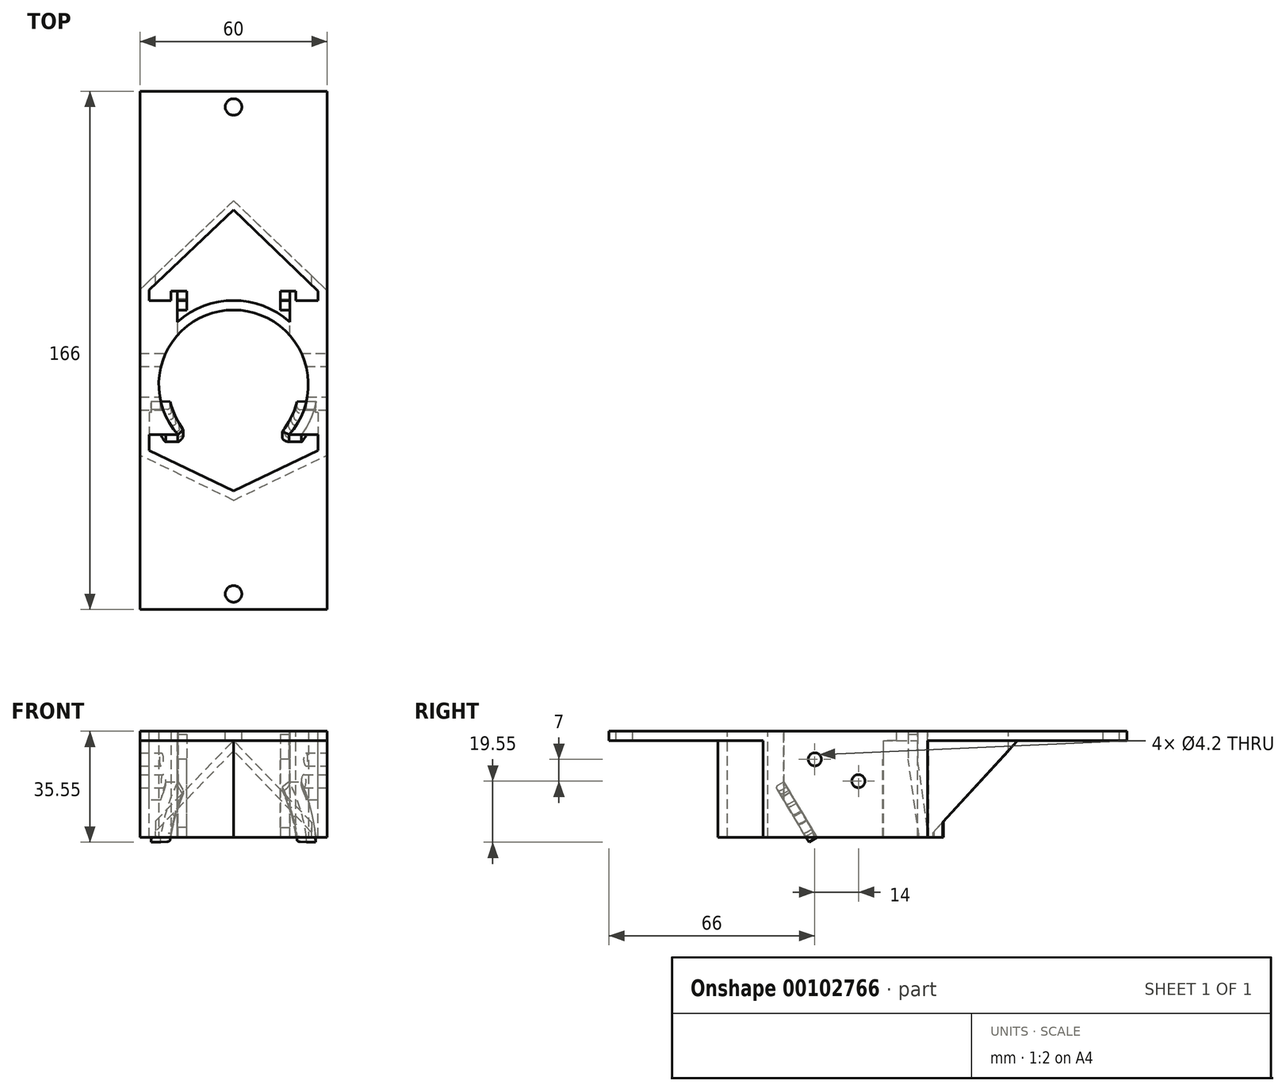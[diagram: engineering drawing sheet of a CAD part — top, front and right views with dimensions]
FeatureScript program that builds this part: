
annotation { "Feature Type Name" : "Feature", "Feature Type Description" : "" }
export const myFeature = defineFeature(function(context is Context, id is Id, definition is map)
    precondition{}
    {
        {
            var Q0;
            Q0=qCreatedBy(makeId("Top.planeOp"),FACE);
            var sketch = newSketch(context, id + "F0", { "sketchPlane" : qUnion([Q0])});
            skArc(sketch, "E0", {"start": v(17.82, -16) * mm, "mid": v(0, 23.95) * mm, "end": v(-17.82, -16) * mm});
            skArc(sketch, "E1", {"start": v(21.75, -16) * mm, "mid": v(0, 27) * mm, "end": v(-21.75, -16) * mm});
            skLineSegment(sketch, "E2", {"start": v(-21.75, -16) * mm, "end": v(-17.82, -16) * mm});
            skLineSegment(sketch, "E3", {"start": v(-17.82, -16) * mm, "end": v(0, -16) * mm, "construction": true});
            skLineSegment(sketch, "E4", {"start": v(0, -16) * mm, "end": v(17.82, -16) * mm, "construction": true});
            skLineSegment(sketch, "E5", {"start": v(17.82, -16) * mm, "end": v(21.75, -16) * mm});
            skLineSegment(sketch, "E6", {"start": v(-39.55, 16) * mm, "end": v(46.97, 16) * mm, "construction": true});
            skLineSegment(sketch, "E7.bottom", {"start": v(-18, 28) * mm, "end": v(18, 28) * mm});
            skLineSegment(sketch, "E7.top", {"start": v(-18, 16) * mm, "end": v(18, 16) * mm});
            skLineSegment(sketch, "E7.left", {"start": v(-18, 28) * mm, "end": v(-18, 16) * mm});
            skLineSegment(sketch, "E7.right", {"start": v(18, 28) * mm, "end": v(18, 16) * mm});
            skLineSegment(sketch, "E8.bottom", {"start": v(-20, 30) * mm, "end": v(20, 30) * mm});
            skLineSegment(sketch, "E8.top", {"start": v(-20, 16) * mm, "end": v(20, 16) * mm});
            skLineSegment(sketch, "E8.left", {"start": v(-20, 30) * mm, "end": v(-20, 16) * mm});
            skLineSegment(sketch, "E8.right", {"start": v(20, 30) * mm, "end": v(20, 16) * mm});
            skLineSegment(sketch, "E9", {"start": v(-18, 28) * mm, "end": v(-18, 30) * mm});
            skLineSegment(sketch, "E10", {"start": v(18, 28) * mm, "end": v(18, 30) * mm});
            skSolve(sketch);
        }
        {
            var Q0;
            {var subQ0=sQuery(id+"F0.wireOp",EDGE,"E5");Q0=makeQuery(id+"F0.imprint","IMPRINT",FACE,{"disambiguationData":[TD([[makeQuery(id+"F0.imprint","IMPRINT",EDGE,{"derivedFrom":subQ0}),1.0]])]});}
            var Q1;
            {var subQ5=sQuery(id+"F0.wireOp",EDGE,"I0pMRqWO-E578-Ecd0-evph-6hkm0RlLLB7E.top");Q1=makeQuery(id+"F0.imprint","IMPRINT",FACE,{"disambiguationData":[TD([[makeQuery(id+"F0.imprint","IMPRINT",EDGE,{"derivedFrom":subQ5}),-1.0]])]});}
            var Q2;
            {var subQ5=sQuery(id+"F0.wireOp",EDGE,"9YEPt3lm-ZwK1-mWlz-v4R1-j5LsX5DvNkkA.top");Q2=makeQuery(id+"F0.imprint","IMPRINT",FACE,{"disambiguationData":[TD([[makeQuery(id+"F0.imprint","IMPRINT",EDGE,{"derivedFrom":subQ5}),1.0]])]});}
            var Q3;
            {var subQ3=sQuery(id+"F0.wireOp",EDGE,"I0pMRqWO-E578-Ecd0-evph-6hkm0RlLLB7E.left");var subQ5=sQuery(id+"F0.wireOp",EDGE,"E1");var subQ6=makeQuery(id+"F0.imprint","INTERSECT",VERTEX,{"derivedFrom":[subQ5,subQ3]});Q3=makeQuery(id+"F0.imprint","IMPRINT",FACE,{"disambiguationData":[TD([[makeQuery(id+"F0.imprint","IMPRINT",EDGE,{"disambiguationData":[TD([[subQ6,-1.0]])],"derivedFrom":subQ5}),1.0]])]});}
            var Q4;
            {var subQ5=sQuery(id+"F0.wireOp",EDGE,"I0pMRqWO-E578-Ecd0-evph-6hkm0RlLLB7E.bottom");Q4=makeQuery(id+"F0.imprint","IMPRINT",FACE,{"disambiguationData":[TD([[makeQuery(id+"F0.imprint","IMPRINT",EDGE,{"derivedFrom":subQ5}),1.0]])]});}
            var Q5;
            {var subQ5=sQuery(id+"F0.wireOp",EDGE,"9YEPt3lm-ZwK1-mWlz-v4R1-j5LsX5DvNkkA.bottom");Q5=makeQuery(id+"F0.imprint","IMPRINT",FACE,{"disambiguationData":[TD([[makeQuery(id+"F0.imprint","IMPRINT",EDGE,{"derivedFrom":subQ5}),-1.0]])]});}
            var Q6;
            {var subQ1=sQuery(id+"F0.wireOp",EDGE,"E2");Q6=makeQuery(id+"F0.imprint","IMPRINT",FACE,{"disambiguationData":[TD([[makeQuery(id+"F0.imprint","IMPRINT",EDGE,{"derivedFrom":subQ1}),1.0]])]});}
            var Q7;
            {var subQ5=sQuery(id+"F0.wireOp",EDGE,"E9");Q7=makeQuery(id+"F0.imprint","IMPRINT",FACE,{"disambiguationData":[TD([[makeQuery(id+"F0.imprint","IMPRINT",EDGE,{"derivedFrom":subQ5}),1.0]])]});}
            var Q8;
            {var subQ5=sQuery(id+"F0.wireOp",EDGE,"E10");Q8=makeQuery(id+"F0.imprint","IMPRINT",FACE,{"disambiguationData":[TD([[makeQuery(id+"F0.imprint","IMPRINT",EDGE,{"derivedFrom":subQ5}),-1.0]])]});}
            var Q9;
            {var subQ0=sQuery(id+"F0.wireOp",EDGE,"E8.top");var subQ8=sQuery(id+"F0.wireOp",EDGE,"E0");var subQ9=makeQuery(id+"F0.imprint","INTERSECT",VERTEX,{"disambiguationData":[OD(0.0)],"derivedFrom":[subQ8,subQ0]});Q9=makeQuery(id+"F0.imprint","IMPRINT",FACE,{"disambiguationData":[TD([[makeQuery(id+"F0.imprint","IMPRINT",EDGE,{"disambiguationData":[TD([[subQ9,-1.0]])],"derivedFrom":subQ8}),-1.0]])]});}
            var Q10;
            {var subQ0=sQuery(id+"F0.wireOp",EDGE,"E8.left");var subQ1=sQuery(id+"F0.wireOp",EDGE,"E1");var subQ2=makeQuery(id+"F0.imprint","INTERSECT",VERTEX,{"derivedFrom":[subQ1,subQ0]});Q10=makeQuery(id+"F0.imprint","IMPRINT",FACE,{"disambiguationData":[TD([[makeQuery(id+"F0.imprint","IMPRINT",EDGE,{"disambiguationData":[TD([[subQ2,1.0]])],"derivedFrom":subQ1}),1.0]])]});}
            var Q11;
            {var subQ0=sQuery(id+"F0.wireOp",EDGE,"E8.right");var subQ1=sQuery(id+"F0.wireOp",EDGE,"E1");var subQ2=makeQuery(id+"F0.imprint","INTERSECT",VERTEX,{"derivedFrom":[subQ1,subQ0]});Q11=makeQuery(id+"F0.imprint","IMPRINT",FACE,{"disambiguationData":[TD([[makeQuery(id+"F0.imprint","IMPRINT",EDGE,{"disambiguationData":[TD([[subQ2,-1.0]])],"derivedFrom":subQ1}),1.0]])]});}
            extrude(context, id + "F1", {"entities" : qUnion([Q0, Q1, Q2, Q3, Q4, Q5, Q6, Q7, Q8, Q9, Q10, Q11]), "depth" : 3 * mm});
        }
        {
            var Q0;
            {var subQ5=sQuery(id+"F0.wireOp",EDGE,"E9");Q0=makeQuery(id+"F0.imprint","IMPRINT",FACE,{"disambiguationData":[TD([[makeQuery(id+"F0.imprint","IMPRINT",EDGE,{"derivedFrom":subQ5}),1.0]])]});}
            var Q1;
            {var subQ5=sQuery(id+"F0.wireOp",EDGE,"E10");Q1=makeQuery(id+"F0.imprint","IMPRINT",FACE,{"disambiguationData":[TD([[makeQuery(id+"F0.imprint","IMPRINT",EDGE,{"derivedFrom":subQ5}),-1.0]])]});}
            var Q2;
            {var subQ0=sQuery(id+"F0.wireOp",EDGE,"E8.left");var subQ1=sQuery(id+"F0.wireOp",EDGE,"E1");var subQ2=makeQuery(id+"F0.imprint","INTERSECT",VERTEX,{"derivedFrom":[subQ1,subQ0]});Q2=makeQuery(id+"F0.imprint","IMPRINT",FACE,{"disambiguationData":[TD([[makeQuery(id+"F0.imprint","IMPRINT",EDGE,{"disambiguationData":[TD([[subQ2,1.0]])],"derivedFrom":subQ1}),1.0]])]});}
            var Q3;
            {var subQ0=sQuery(id+"F0.wireOp",EDGE,"E8.right");var subQ1=sQuery(id+"F0.wireOp",EDGE,"E1");var subQ2=makeQuery(id+"F0.imprint","INTERSECT",VERTEX,{"derivedFrom":[subQ1,subQ0]});Q3=makeQuery(id+"F0.imprint","IMPRINT",FACE,{"disambiguationData":[TD([[makeQuery(id+"F0.imprint","IMPRINT",EDGE,{"disambiguationData":[TD([[subQ2,-1.0]])],"derivedFrom":subQ1}),1.0]])]});}
            extrude(context, id + "F2", {"entities" : qUnion([Q0, Q1, Q2, Q3]), "operationType" : NewBodyOperationType.ADD, "oppositeDirection" : true, "depth" : 6 * mm});
        }
        {
            var Q0;
            Q0=qCreatedBy(makeId("Top.planeOp"),FACE);
            var sketch = newSketch(context, id + "F3", { "sketchPlane" : qUnion([Q0])});
            skLineSegment(sketch, "E11", {"start": v(-34.3, 23.95) * mm, "end": v(29.7, 23.95) * mm, "construction": true});
            skLineSegment(sketch, "E12.bottom", {"start": v(-18, 23.95) * mm, "end": v(-15, 23.95) * mm});
            skLineSegment(sketch, "E12.top", {"start": v(-18, 26.95) * mm, "end": v(-15, 26.95) * mm});
            skLineSegment(sketch, "E12.left", {"start": v(-18, 23.95) * mm, "end": v(-18, 26.95) * mm});
            skLineSegment(sketch, "E12.right", {"start": v(-15, 23.95) * mm, "end": v(-15, 26.95) * mm});
            skLineSegment(sketch, "E13.bottom", {"start": v(15, 23.95) * mm, "end": v(18, 23.95) * mm});
            skLineSegment(sketch, "E13.top", {"start": v(15, 26.95) * mm, "end": v(18, 26.95) * mm});
            skLineSegment(sketch, "E13.left", {"start": v(15, 23.95) * mm, "end": v(15, 26.95) * mm});
            skLineSegment(sketch, "E13.right", {"start": v(18, 23.95) * mm, "end": v(18, 26.95) * mm});
            skSolve(sketch);
        }
        {
            var Q0;
            Q0=makeQuery(id+"F3.imprint","IMPRINT",FACE,{"disambiguationData":[TD([[makeQuery(id+"F3.imprint","IMPRINT",EDGE,{"derivedFrom":sQuery(id+"F3.wireOp",EDGE,"E12.bottom")}),1.0]])]});
            var Q1;
            Q1=makeQuery(id+"F3.imprint","IMPRINT",FACE,{"disambiguationData":[TD([[makeQuery(id+"F3.imprint","IMPRINT",EDGE,{"derivedFrom":sQuery(id+"F3.wireOp",EDGE,"E13.bottom")}),1.0]])]});
            extrude(context, id + "F4", {"entities" : qUnion([Q0, Q1]), "operationType" : NewBodyOperationType.ADD, "depth" : 2 * mm});
        }
        {
            var Q0;
            Q0=makeQuery(id+"F3.imprint","IMPRINT",FACE,{"disambiguationData":[TD([[makeQuery(id+"F3.imprint","IMPRINT",EDGE,{"derivedFrom":sQuery(id+"F3.wireOp",EDGE,"E12.bottom")}),1.0]])]});
            var Q1;
            Q1=makeQuery(id+"F3.imprint","IMPRINT",FACE,{"disambiguationData":[TD([[makeQuery(id+"F3.imprint","IMPRINT",EDGE,{"derivedFrom":sQuery(id+"F3.wireOp",EDGE,"E13.bottom")}),1.0]])]});
            var Q2;
            Q2=makeQuery(id+"F2.opExtrude","CAP_FACE",FACE,{"disambiguationData":[OSD([sQuery(id+"F0.wireOp",EDGE,"E7.left"),sQuery(id+"F0.wireOp",EDGE,"E8.bottom"),sQuery(id+"F0.wireOp",EDGE,"E8.top"),sQuery(id+"F0.wireOp",EDGE,"E8.left"),sQuery(id+"F0.wireOp",EDGE,"E9")])],"isStart":false});
            extrude(context, id + "F5", {"entities" : qUnion([Q0, Q1]), "operationType" : NewBodyOperationType.ADD, "endBound" : BoundingType.UP_TO_SURFACE, "oppositeDirection" : true, "endBoundEntityFace" : qUnion([Q2]), "depth" : 4 * mm});
        }
        {
            var Q0;
            {var subQ0=sQuery(id+"F0.wireOp",EDGE,"E2");Q0=makeQuery(id+"F0.imprint","IMPRINT",FACE,{"disambiguationData":[TD([[makeQuery(id+"F0.imprint","IMPRINT",EDGE,{"derivedFrom":subQ0}),1.0]])]});}
            var Q1;
            {var subQ4=sQuery(id+"F0.wireOp",EDGE,"E5");Q1=makeQuery(id+"F0.imprint","IMPRINT",FACE,{"disambiguationData":[TD([[makeQuery(id+"F0.imprint","IMPRINT",EDGE,{"derivedFrom":subQ4}),1.0]])]});}
            extrude(context, id + "F6", {"entities" : qUnion([Q0, Q1]), "operationType" : NewBodyOperationType.ADD, "oppositeDirection" : true, "depth" : 6 * mm});
        }
        {
            var Q0;
            {var subQ0=sQuery(id+"F0.wireOp",EDGE,"E8.left");Q0=makeQuery(id+"F2.boolean.opBoolean","MERGE",FACE,{"derivedFrom":[makeQuery(id+"F1.opExtrude","SWEPT_FACE",FACE,{"disambiguationData":[OSD([subQ0])]}),makeQuery(id+"F2.opExtrude","SWEPT_FACE",FACE,{"disambiguationData":[OSD([subQ0])]})]});}
            var sketch = newSketch(context, id + "F7", { "sketchPlane" : qUnion([Q0])});
            skLineSegment(sketch, "E14", {"start": v(-23.95, 16.95) * mm, "end": v(-23.95, -28.82) * mm, "construction": true});
            skLineSegment(sketch, "E15.bottom", {"start": v(-30, -6) * mm, "end": v(-18.14, -6) * mm});
            skLineSegment(sketch, "E15.top", {"start": v(-30, -31) * mm, "end": v(-18.14, -31) * mm});
            skLineSegment(sketch, "E15.left", {"start": v(-30, -6) * mm, "end": v(-30, -31) * mm});
            skLineSegment(sketch, "E15.right", {"start": v(-18.14, -6) * mm, "end": v(-18.14, -31) * mm});
            skLineSegment(sketch, "E16", {"start": v(-27.45, 14.9) * mm, "end": v(-27.45, -40.68) * mm, "construction": true});
            skLineSegment(sketch, "E17", {"start": v(-23.95, -6) * mm, "end": v(-27.45, -31) * mm});
            skLineSegment(sketch, "E18", {"start": v(-26.95, -6) * mm, "end": v(-30.45, -31) * mm});
            skLineSegment(sketch, "E19", {"start": v(-30.45, -31) * mm, "end": v(-30, -31) * mm});
            skSolve(sketch);
        }
        {
            var Q0;
            {var subQ0=sQuery(id+"F7.wireOp",EDGE,"E17");Q0=makeQuery(id+"F7.imprint","IMPRINT",FACE,{"disambiguationData":[TD([[makeQuery(id+"F7.imprint","IMPRINT",EDGE,{"derivedFrom":subQ0}),-1.0]])]});}
            var Q1;
            {var subQ0=sQuery(id+"F3.wireOp",EDGE,"E12.right");Q1=makeQuery(id+"F5.boolean.opBoolean","MERGE",FACE,{"derivedFrom":[makeQuery(id+"F4.opExtrude","SWEPT_FACE",FACE,{"disambiguationData":[OSD([subQ0])]}),makeQuery(id+"F5.opExtrude","SWEPT_FACE",FACE,{"disambiguationData":[OSD([subQ0])]})]});}
            extrude(context, id + "F8", {"entities" : qUnion([Q0]), "operationType" : NewBodyOperationType.ADD, "endBound" : BoundingType.UP_TO_SURFACE, "oppositeDirection" : true, "endBoundEntityFace" : qUnion([Q1]), "depth" : 25 * mm});
        }
        {
            var Q0;
            {var subQ0=sQuery(id+"F7.wireOp",EDGE,"E15.right");Q0=makeQuery(id+"F7.imprint","IMPRINT",FACE,{"disambiguationData":[TD([[makeQuery(id+"F7.imprint","IMPRINT",EDGE,{"derivedFrom":subQ0}),-1.0]])]});}
            var Q1;
            {var subQ1=sQuery(id+"F7.wireOp",EDGE,"E15.bottom");var subQ5=sQuery(id+"F7.wireOp",EDGE,"E18");var subQ6=makeQuery(id+"F7.imprint","INTERSECT",VERTEX,{"derivedFrom":[subQ1,subQ5]});Q1=makeQuery(id+"F7.imprint","IMPRINT",FACE,{"disambiguationData":[TD([[makeQuery(id+"F7.imprint","IMPRINT",EDGE,{"disambiguationData":[TD([[subQ6,-1.0]])],"derivedFrom":subQ5}),-1.0]])]});}
            var Q2;
            {var subQ0=sQuery(id+"F7.wireOp",EDGE,"E17");Q2=makeQuery(id+"F7.imprint","IMPRINT",FACE,{"disambiguationData":[TD([[makeQuery(id+"F7.imprint","IMPRINT",EDGE,{"derivedFrom":subQ0}),-1.0]])]});}
            extrude(context, id + "F9", {"entities" : qUnion([Q0, Q1, Q2]), "operationType" : NewBodyOperationType.ADD, "oppositeDirection" : true, "depth" : 2 * mm});
        }
        {
            var Q0;
            {var subQ0=sQuery(id+"F0.wireOp",EDGE,"E8.right");Q0=makeQuery(id+"F2.boolean.opBoolean","MERGE",FACE,{"derivedFrom":[makeQuery(id+"F1.opExtrude","SWEPT_FACE",FACE,{"disambiguationData":[OSD([subQ0])]}),makeQuery(id+"F2.opExtrude","SWEPT_FACE",FACE,{"disambiguationData":[OSD([subQ0])]})]});}
            var sketch = newSketch(context, id + "F10", { "sketchPlane" : qUnion([Q0])});
            skLineSegment(sketch, "E20", {"start": v(23.95, -6) * mm, "end": v(27.45, -31) * mm});
            skLineSegment(sketch, "E21", {"start": v(27.45, -31) * mm, "end": v(30.45, -31) * mm});
            skLineSegment(sketch, "E22", {"start": v(30.45, -31) * mm, "end": v(26.95, -6) * mm});
            skLineSegment(sketch, "E23", {"start": v(26.95, -6) * mm, "end": v(23.95, -6) * mm});
            skLineSegment(sketch, "E24.bottom", {"start": v(18.14, -6) * mm, "end": v(30, -6) * mm});
            skLineSegment(sketch, "E24.top", {"start": v(18.14, -31) * mm, "end": v(30, -31) * mm});
            skLineSegment(sketch, "E24.left", {"start": v(18.14, -6) * mm, "end": v(18.14, -31) * mm});
            skLineSegment(sketch, "E24.right", {"start": v(30, -6) * mm, "end": v(30, -31) * mm});
            skSolve(sketch);
        }
        {
            var Q0;
            {var subQ0=sQuery(id+"F10.wireOp",EDGE,"E20");Q0=makeQuery(id+"F10.imprint","IMPRINT",FACE,{"disambiguationData":[TD([[makeQuery(id+"F10.imprint","IMPRINT",EDGE,{"derivedFrom":subQ0}),-1.0]])]});}
            var Q1;
            {var subQ1=sQuery(id+"F10.wireOp",EDGE,"E20");Q1=makeQuery(id+"F10.imprint","IMPRINT",FACE,{"disambiguationData":[TD([[makeQuery(id+"F10.imprint","IMPRINT",EDGE,{"derivedFrom":subQ1}),1.0]])]});}
            var Q2;
            {var subQ0=sQuery(id+"F10.wireOp",EDGE,"E24.bottom");var subQ1=sQuery(id+"F10.wireOp",EDGE,"E22");var subQ2=makeQuery(id+"F10.imprint","INTERSECT",VERTEX,{"derivedFrom":[subQ1,subQ0]});Q2=makeQuery(id+"F10.imprint","IMPRINT",FACE,{"disambiguationData":[TD([[makeQuery(id+"F10.imprint","IMPRINT",EDGE,{"disambiguationData":[TD([[subQ2,1.0]])],"derivedFrom":subQ1}),-1.0]])]});}
            var Q3;
            {var subQ0=sQuery(id+"F0.wireOp",EDGE,"E10");var subQ1=sQuery(id+"F0.wireOp",EDGE,"E7.right");Q3=makeQuery(id+"F2.boolean.opBoolean","MERGE",FACE,{"derivedFrom":[makeQuery(id+"F1.opExtrude","SWEPT_FACE",FACE,{"disambiguationData":[OSD([subQ1,subQ0])]}),makeQuery(id+"F2.opExtrude","SWEPT_FACE",FACE,{"disambiguationData":[OSD([subQ1,subQ0])]})]});}
            extrude(context, id + "F11", {"entities" : qUnion([Q0, Q1, Q2]), "operationType" : NewBodyOperationType.ADD, "endBound" : BoundingType.UP_TO_SURFACE, "oppositeDirection" : true, "endBoundEntityFace" : qUnion([Q3]), "depth" : 25 * mm});
        }
        {
            var Q0;
            {var subQ1=sQuery(id+"F10.wireOp",EDGE,"E20");Q0=makeQuery(id+"F10.imprint","IMPRINT",FACE,{"disambiguationData":[TD([[makeQuery(id+"F10.imprint","IMPRINT",EDGE,{"derivedFrom":subQ1}),1.0]])]});}
            var Q1;
            {var subQ0=sQuery(id+"F3.wireOp",EDGE,"E13.left");Q1=makeQuery(id+"F5.boolean.opBoolean","MERGE",FACE,{"derivedFrom":[makeQuery(id+"F4.opExtrude","SWEPT_FACE",FACE,{"disambiguationData":[OSD([subQ0])]}),makeQuery(id+"F5.opExtrude","SWEPT_FACE",FACE,{"disambiguationData":[OSD([subQ0])]})]});}
            extrude(context, id + "F12", {"entities" : qUnion([Q0]), "operationType" : NewBodyOperationType.ADD, "endBound" : BoundingType.UP_TO_SURFACE, "oppositeDirection" : true, "endBoundEntityFace" : qUnion([Q1]), "depth" : 25 * mm});
        }
        {
            var Q0;
            {var subQ0=sQuery(id+"F0.wireOp",EDGE,"E0");var subQ1=sQuery(id+"F0.wireOp",EDGE,"E8.top");var subQ2=sQuery(id+"F3.wireOp",EDGE,"E12.bottom");var subQ3=sQuery(id+"F0.wireOp",EDGE,"E8.left");var subQ4=sQuery(id+"F0.wireOp",EDGE,"E9");var subQ5=sQuery(id+"F0.wireOp",EDGE,"E7.left");var subQ6=sQuery(id+"F0.wireOp",EDGE,"E2");var subQ7=sQuery(id+"F0.wireOp",EDGE,"E1");var subQ12=sQuery(id+"F0.wireOp",EDGE,"E8.bottom");Q0=makeQuery(id+"F8.boolean.opBoolean","SPLIT",FACE,{"disambiguationData":[TD([makeQuery(id+"F1.opExtrude","SWEPT_FACE",FACE,{"disambiguationData":[OSD([subQ0])]})])],"derivedFrom":makeQuery(id+"F6.boolean.opBoolean","MERGE",FACE,{"derivedFrom":[makeQuery(id+"F5.boolean.opBoolean","MERGE",FACE,{"derivedFrom":[makeQuery(id+"F2.opExtrude","CAP_FACE",FACE,{"disambiguationData":[OSD([subQ5,subQ12,subQ1,subQ3,subQ4])],"isStart":false}),makeQuery(id+"F5.opExtrude","CAP_FACE",FACE,{"disambiguationData":[OSD([subQ5,subQ12,subQ1,subQ3,subQ4]),ownerDisambiguation([makeQuery(id+"F5.opExtrude","SWEPT_BODY",BODY,{"disambiguationData":[OSD([subQ2,sQuery(id+"F3.wireOp",EDGE,"E12.top"),sQuery(id+"F3.wireOp",EDGE,"E12.left"),sQuery(id+"F3.wireOp",EDGE,"E12.right")])]})])],"isStart":false})]}),makeQuery(id+"F6.opExtrude","CAP_FACE",FACE,{"disambiguationData":[OSD([subQ0,subQ7,subQ6,subQ1,subQ3])],"isStart":false})]})});}
            var sketch = newSketch(context, id + "F13", { "sketchPlane" : qUnion([Q0])});
            skArc(sketch, "E25", {"start": v(-17.82, 16) * mm, "mid": v(-23.9, -1.53) * mm, "end": v(-15.64, -18.14) * mm});
            skArc(sketch, "E26", {"start": v(-21.75, 16) * mm, "mid": v(-26.96, -1.38) * mm, "end": v(-20, -18.14) * mm});
            skLineSegment(sketch, "E27", {"start": v(-36.94, 16) * mm, "end": v(37.61, 16) * mm, "construction": true});
            skLineSegment(sketch, "E28", {"start": v(-44, -18.14) * mm, "end": v(46.28, -18.14) * mm, "construction": true});
            skArc(sketch, "E29.trimOffspring", {"start": v(15.64, -18.14) * mm, "mid": v(23.9, -1.53) * mm, "end": v(17.82, 16) * mm});
            skArc(sketch, "E30.trimOffspring", {"start": v(20, -18.14) * mm, "mid": v(26.96, -1.38) * mm, "end": v(21.75, 16) * mm});
            skLineSegment(sketch, "E31", {"start": v(-21.75, 16) * mm, "end": v(-17.82, 16) * mm});
            skLineSegment(sketch, "E32", {"start": v(17.82, 16) * mm, "end": v(21.75, 16) * mm});
            skLineSegment(sketch, "E33", {"start": v(15.64, -18.14) * mm, "end": v(20, -18.14) * mm});
            skLineSegment(sketch, "E34", {"start": v(-20, -18.14) * mm, "end": v(-15.64, -18.14) * mm});
            skLineSegment(sketch, "E35", {"start": v(18, -14.37) * mm, "end": v(18, -22.26) * mm});
            skSolve(sketch);
        }
        {
            var Q0;
            {var subQ1=sQuery(id+"F13.wireOp",EDGE,"E30.trimOffspring");Q0=makeQuery(id+"F13.imprint","IMPRINT",FACE,{"disambiguationData":[TD([[makeQuery(id+"F13.imprint","IMPRINT",EDGE,{"derivedFrom":subQ1}),1.0]])]});}
            var Q1;
            {var subQ1=sQuery(id+"F13.wireOp",EDGE,"E26");Q1=makeQuery(id+"F13.imprint","IMPRINT",FACE,{"disambiguationData":[TD([[makeQuery(id+"F13.imprint","IMPRINT",EDGE,{"derivedFrom":subQ1}),-1.0]])]});}
            var Q2;
            {var subQ0=sQuery(id+"F10.wireOp",EDGE,"E24.top");Q2=makeQuery(id+"F12.boolean.opBoolean","MERGE",FACE,{"derivedFrom":[makeQuery(id+"F11.opExtrude","SWEPT_FACE",FACE,{"disambiguationData":[OSD([subQ0])]}),makeQuery(id+"F12.opExtrude","SWEPT_FACE",FACE,{"disambiguationData":[OSD([subQ0])]})]});}
            extrude(context, id + "F14", {"entities" : qUnion([Q0, Q1]), "operationType" : NewBodyOperationType.ADD, "endBound" : BoundingType.UP_TO_SURFACE, "endBoundEntityFace" : qUnion([Q2]), "depth" : 25 * mm});
        }
        {
            var Q0;
            Q0=qCreatedBy(makeId("Right.planeOp"),FACE);
            var sketch = newSketch(context, id + "F15", { "sketchPlane" : qUnion([Q0])});
            skLineSegment(sketch, "E36", {"start": v(-39.62, 3) * mm, "end": v(37.43, 3) * mm, "construction": true});
            skLineSegment(sketch, "E37", {"start": v(-39.2, -13.2) * mm, "end": v(35.91, -13.2) * mm, "construction": true});
            skLineSegment(sketch, "E38", {"start": v(-16, -13.2) * mm, "end": v(-5.3, -31) * mm});
            skLineSegment(sketch, "E39", {"start": v(-16, -13.2) * mm, "end": v(-16, -31) * mm});
            skLineSegment(sketch, "E40", {"start": v(-16, -31) * mm, "end": v(-5.3, -31) * mm});
            skSolve(sketch);
        }
        {
            var Q0;
            Q0=makeQuery(id+"F15.imprint","IMPRINT",FACE,{"disambiguationData":[TD([[makeQuery(id+"F15.imprint","IMPRINT",EDGE,{"derivedFrom":sQuery(id+"F15.wireOp",EDGE,"E38")}),-1.0]])]});
            extrude(context, id + "F16", {"entities" : qUnion([Q0]), "operationType" : NewBodyOperationType.REMOVE, "endBound" : BoundingType.SYMMETRIC, "oppositeDirection" : true, "depth" : 60 * mm});
        }
        {
            var Q0;
            {var subQ0=sQuery(id+"F0.wireOp",EDGE,"E2");Q0=makeQuery(id+"F16.boolean.opBoolean","COPY",FACE,{"disambiguationData":[TD([makeQuery(id+"F1.opExtrude","SWEPT_FACE",FACE,{"disambiguationData":[OSD([subQ0])]})])],"derivedFrom":makeQuery(id+"F16.opExtrude","SWEPT_FACE",FACE,{"disambiguationData":[OSD([sQuery(id+"F15.wireOp",EDGE,"E38")])]})});}
            var sketch = newSketch(context, id + "F17", { "sketchPlane" : qUnion([Q0])});
            skLineSegment(sketch, "E41", {"start": v(-21.75, -3.07) * mm, "end": v(-23.33, -7.76) * mm});
            skLineSegment(sketch, "E42", {"start": v(-23.33, -7.76) * mm, "end": v(-24.67, -12.85) * mm});
            skLineSegment(sketch, "E43", {"start": v(-24.67, -12.85) * mm, "end": v(-25.68, -17.96) * mm});
            skLineSegment(sketch, "E44", {"start": v(-25.68, -17.96) * mm, "end": v(-26.22, -21.6) * mm});
            skLineSegment(sketch, "E45", {"start": v(-26.22, -21.6) * mm, "end": v(-26.47, -23.84) * mm});
            skLineSegment(sketch, "E46", {"start": v(-26.47, -23.84) * mm, "end": v(-23.36, -23.84) * mm});
            skLineSegment(sketch, "E47", {"start": v(-23.36, -23.84) * mm, "end": v(-22.89, -20.45) * mm});
            skLineSegment(sketch, "E48", {"start": v(-22.89, -20.45) * mm, "end": v(-22.28, -17.06) * mm});
            skLineSegment(sketch, "E49", {"start": v(-22.28, -17.06) * mm, "end": v(-21.41, -13.3) * mm});
            skLineSegment(sketch, "E50", {"start": v(-21.41, -13.3) * mm, "end": v(-20.37, -9.68) * mm});
            skLineSegment(sketch, "E51", {"start": v(-20.37, -9.68) * mm, "end": v(-19.34, -6.72) * mm});
            skLineSegment(sketch, "E52", {"start": v(-19.34, -6.72) * mm, "end": v(-17.82, -3.07) * mm});
            skLineSegment(sketch, "E53", {"start": v(-17.82, -3.07) * mm, "end": v(-21.75, -3.07) * mm});
            skLineSegment(sketch, "E54", {"start": v(-14.82, -3.07) * mm, "end": v(-16.34, -6.94) * mm});
            skLineSegment(sketch, "E55", {"start": v(-16.34, -6.94) * mm, "end": v(-17.4, -10.05) * mm});
            skLineSegment(sketch, "E56", {"start": v(-17.4, -10.05) * mm, "end": v(-18.48, -13.93) * mm});
            skLineSegment(sketch, "E57", {"start": v(-18.48, -13.93) * mm, "end": v(-19.32, -17.55) * mm});
            skLineSegment(sketch, "E58", {"start": v(-19.32, -17.55) * mm, "end": v(-19.9, -20.76) * mm});
            skLineSegment(sketch, "E59", {"start": v(-19.9, -20.76) * mm, "end": v(-20.36, -23.63) * mm});
            skLineSegment(sketch, "E60", {"start": v(-20.36, -23.63) * mm, "end": v(-23.36, -23.84) * mm});
            skLineSegment(sketch, "E61", {"start": v(-14.82, -3.07) * mm, "end": v(-17.82, -3.07) * mm});
            skLineSegment(sketch, "E62", {"start": v(21.75, -3.07) * mm, "end": v(17.82, -3.07) * mm});
            skLineSegment(sketch, "E63", {"start": v(17.82, -3.07) * mm, "end": v(19.36, -6.75) * mm});
            skLineSegment(sketch, "E64", {"start": v(19.36, -6.75) * mm, "end": v(20.66, -10.62) * mm});
            skLineSegment(sketch, "E65", {"start": v(20.66, -10.62) * mm, "end": v(21.55, -13.84) * mm});
            skLineSegment(sketch, "E66", {"start": v(21.55, -13.84) * mm, "end": v(22.27, -17) * mm});
            skLineSegment(sketch, "E67", {"start": v(22.27, -17) * mm, "end": v(22.8, -19.87) * mm});
            skLineSegment(sketch, "E68", {"start": v(22.8, -19.87) * mm, "end": v(23.36, -23.84) * mm});
            skLineSegment(sketch, "E69", {"start": v(23.36, -23.84) * mm, "end": v(26.34, -23.84) * mm});
            skLineSegment(sketch, "E70", {"start": v(26.34, -23.84) * mm, "end": v(26.09, -20.73) * mm});
            skLineSegment(sketch, "E71", {"start": v(26.09, -20.73) * mm, "end": v(25.67, -18.04) * mm});
            skLineSegment(sketch, "E72", {"start": v(25.67, -18.04) * mm, "end": v(25.16, -15.17) * mm});
            skLineSegment(sketch, "E73", {"start": v(25.16, -15.17) * mm, "end": v(24.6, -12.67) * mm});
            skLineSegment(sketch, "E74", {"start": v(24.6, -12.67) * mm, "end": v(23.97, -10.06) * mm});
            skLineSegment(sketch, "E75", {"start": v(23.97, -10.06) * mm, "end": v(23.2, -7.33) * mm});
            skLineSegment(sketch, "E76", {"start": v(23.2, -7.33) * mm, "end": v(22.37, -4.9) * mm});
            skLineSegment(sketch, "E77", {"start": v(22.37, -4.9) * mm, "end": v(21.75, -3.07) * mm});
            skLineSegment(sketch, "E78", {"start": v(17.82, -3.07) * mm, "end": v(14.82, -3.07) * mm});
            skLineSegment(sketch, "E79", {"start": v(14.82, -3.07) * mm, "end": v(16.37, -7.03) * mm});
            skLineSegment(sketch, "E80", {"start": v(16.37, -7.03) * mm, "end": v(17.7, -11.04) * mm});
            skLineSegment(sketch, "E81", {"start": v(17.7, -11.04) * mm, "end": v(18.6, -14.4) * mm});
            skLineSegment(sketch, "E82", {"start": v(18.6, -14.4) * mm, "end": v(19.28, -17.27) * mm});
            skLineSegment(sketch, "E83", {"start": v(19.28, -17.27) * mm, "end": v(20.1, -21.81) * mm});
            skLineSegment(sketch, "E84", {"start": v(20.1, -21.81) * mm, "end": v(20.36, -23.65) * mm});
            skLineSegment(sketch, "E85", {"start": v(20.36, -23.65) * mm, "end": v(23.36, -23.84) * mm});
            skPoint(sketch, "E86", {"position": v(19.82, -20.23) * mm});
            skSolve(sketch);
        }
        {
            var Q0;
            Q0=makeQuery(id+"F17.imprint","IMPRINT",FACE,{"disambiguationData":[TD([[makeQuery(id+"F17.imprint","IMPRINT",EDGE,{"derivedFrom":sQuery(id+"F17.wireOp",EDGE,"E47")}),-1.0]])]});
            var Q1;
            Q1=makeQuery(id+"F17.imprint","IMPRINT",FACE,{"disambiguationData":[TD([[makeQuery(id+"F17.imprint","IMPRINT",EDGE,{"derivedFrom":sQuery(id+"F17.wireOp",EDGE,"E63")}),-1.0]])]});
            var Q2;
            Q2=makeQuery(id+"F17.imprint","IMPRINT",FACE,{"disambiguationData":[TD([[makeQuery(id+"F17.imprint","IMPRINT",EDGE,{"derivedFrom":sQuery(id+"F17.wireOp",EDGE,"E62")}),1.0]])]});
            var Q3;
            Q3=makeQuery(id+"F17.imprint","IMPRINT",FACE,{"disambiguationData":[TD([[makeQuery(id+"F17.imprint","IMPRINT",EDGE,{"derivedFrom":sQuery(id+"F17.wireOp",EDGE,"E41")}),1.0]])]});
            var Q4;
            {var subQ0=sQuery(id+"F0.wireOp",EDGE,"E2");Q4=makeQuery(id+"F16.boolean.opBoolean","COPY",FACE,{"disambiguationData":[TD([makeQuery(id+"F1.opExtrude","SWEPT_FACE",FACE,{"disambiguationData":[OSD([subQ0])]})])],"derivedFrom":makeQuery(id+"F16.opExtrude","SWEPT_FACE",FACE,{"disambiguationData":[OSD([sQuery(id+"F15.wireOp",EDGE,"E38")])]})});}
            var Q5;
            {var subQ0=sQuery(id+"F17.wireOp",EDGE,"E45");Q5=makeQuery(id+"F17.imprint","IMPRINT",FACE,{"disambiguationData":[TD([[makeQuery(id+"F17.imprint","IMPRINT",EDGE,{"derivedFrom":subQ0}),-1.0]])]});}
            var Q6;
            {var subQ0=sQuery(id+"F17.wireOp",EDGE,"E41");Q6=makeQuery(id+"F17.imprint","IMPRINT",FACE,{"disambiguationData":[TD([[makeQuery(id+"F17.imprint","IMPRINT",EDGE,{"derivedFrom":subQ0}),-1.0]])]});}
            var Q7;
            {var subQ0=sQuery(id+"F17.wireOp",EDGE,"E50");Q7=makeQuery(id+"F17.imprint","IMPRINT",FACE,{"disambiguationData":[TD([[makeQuery(id+"F17.imprint","IMPRINT",EDGE,{"derivedFrom":subQ0}),1.0]])]});}
            var Q8;
            {var subQ0=sQuery(id+"F17.wireOp",EDGE,"E48");Q8=makeQuery(id+"F17.imprint","IMPRINT",FACE,{"disambiguationData":[TD([[makeQuery(id+"F17.imprint","IMPRINT",EDGE,{"derivedFrom":subQ0}),1.0]])]});}
            var Q9;
            {var subQ0=sQuery(id+"F17.wireOp",EDGE,"E51");Q9=makeQuery(id+"F17.imprint","IMPRINT",FACE,{"disambiguationData":[TD([[makeQuery(id+"F17.imprint","IMPRINT",EDGE,{"derivedFrom":subQ0}),1.0]])]});}
            var Q10;
            {var subQ0=sQuery(id+"F17.wireOp",EDGE,"E49");Q10=makeQuery(id+"F17.imprint","IMPRINT",FACE,{"disambiguationData":[TD([[makeQuery(id+"F17.imprint","IMPRINT",EDGE,{"derivedFrom":subQ0}),1.0]])]});}
            var Q11;
            {var subQ0=sQuery(id+"F17.wireOp",EDGE,"E42");Q11=makeQuery(id+"F17.imprint","IMPRINT",FACE,{"disambiguationData":[TD([[makeQuery(id+"F17.imprint","IMPRINT",EDGE,{"derivedFrom":subQ0}),-1.0]])]});}
            var Q12;
            {var subQ0=sQuery(id+"F17.wireOp",EDGE,"E44");Q12=makeQuery(id+"F17.imprint","IMPRINT",FACE,{"disambiguationData":[TD([[makeQuery(id+"F17.imprint","IMPRINT",EDGE,{"derivedFrom":subQ0}),-1.0]])]});}
            var Q13;
            {var subQ0=sQuery(id+"F17.wireOp",EDGE,"E43");Q13=makeQuery(id+"F17.imprint","IMPRINT",FACE,{"disambiguationData":[TD([[makeQuery(id+"F17.imprint","IMPRINT",EDGE,{"derivedFrom":subQ0}),-1.0]])]});}
            var Q14;
            {var subQ0=sQuery(id+"F17.wireOp",EDGE,"E47");Q14=makeQuery(id+"F17.imprint","IMPRINT",FACE,{"disambiguationData":[TD([[makeQuery(id+"F17.imprint","IMPRINT",EDGE,{"derivedFrom":subQ0}),1.0]])]});}
            var Q15;
            {var subQ0=sQuery(id+"F17.wireOp",EDGE,"E52");Q15=makeQuery(id+"F17.imprint","IMPRINT",FACE,{"disambiguationData":[TD([[makeQuery(id+"F17.imprint","IMPRINT",EDGE,{"derivedFrom":subQ0}),1.0]])]});}
            extrude(context, id + "F18", {"entities" : qUnion([Q0, Q1, Q2, Q3, Q4, Q5, Q6, Q7, Q8, Q9, Q10, Q11, Q12, Q13, Q14, Q15]), "operationType" : NewBodyOperationType.ADD, "depth" : 3 * mm});
        }
        {
            var Q0;
            Q0=makeQuery(id+"F18.opExtrude","CAP_FACE",FACE,{"disambiguationData":[OSD([sQuery(id+"F17.wireOp",EDGE,"E62"),sQuery(id+"F17.wireOp",EDGE,"E69"),sQuery(id+"F17.wireOp",EDGE,"E70"),sQuery(id+"F17.wireOp",EDGE,"E71"),sQuery(id+"F17.wireOp",EDGE,"E72"),sQuery(id+"F17.wireOp",EDGE,"E73"),sQuery(id+"F17.wireOp",EDGE,"E74"),sQuery(id+"F17.wireOp",EDGE,"E75"),sQuery(id+"F17.wireOp",EDGE,"E76"),sQuery(id+"F17.wireOp",EDGE,"E77"),sQuery(id+"F17.wireOp",EDGE,"E78"),sQuery(id+"F17.wireOp",EDGE,"E79"),sQuery(id+"F17.wireOp",EDGE,"E80"),sQuery(id+"F17.wireOp",EDGE,"E81"),sQuery(id+"F17.wireOp",EDGE,"E82"),sQuery(id+"F17.wireOp",EDGE,"E83"),sQuery(id+"F17.wireOp",EDGE,"E84"),sQuery(id+"F17.wireOp",EDGE,"E85")])],"isStart":false});
            var sketch = newSketch(context, id + "F19", { "sketchPlane" : qUnion([Q0])});
            skLineSegment(sketch, "E87", {"start": v(17.82, -3.07) * mm, "end": v(15.6, -5.05) * mm});
            skLineSegment(sketch, "E88", {"start": v(15.6, -5.05) * mm, "end": v(13.86, -3.11) * mm});
            skLineSegment(sketch, "E89", {"start": v(13.86, -3.11) * mm, "end": v(16.33, -2.73) * mm});
            skLineSegment(sketch, "E90", {"start": v(16.33, -2.73) * mm, "end": v(17.82, -3.07) * mm});
            skLineSegment(sketch, "E91", {"start": v(-17.84, -3.07) * mm, "end": v(-16.09, -6.3) * mm});
            skLineSegment(sketch, "E92", {"start": v(-16.09, -6.3) * mm, "end": v(-13.57, -2.73) * mm});
            skLineSegment(sketch, "E93", {"start": v(-13.57, -2.73) * mm, "end": v(-17.57, -2.73) * mm});
            skLineSegment(sketch, "E94", {"start": v(-17.57, -2.73) * mm, "end": v(-17.84, -3.07) * mm});
            skSolve(sketch);
        }
        {
            var Q0;
            Q0=makeQuery(id+"F19.imprint","IMPRINT",FACE,{"disambiguationData":[TD([[makeQuery(id+"F19.imprint","IMPRINT",EDGE,{"derivedFrom":sQuery(id+"F19.wireOp",EDGE,"E91")}),1.0]])]});
            var Q1;
            {var subQ0=sQuery(id+"F19.wireOp",EDGE,"E87");Q1=makeQuery(id+"F19.imprint","IMPRINT",FACE,{"disambiguationData":[TD([[makeQuery(id+"F19.imprint","IMPRINT",EDGE,{"derivedFrom":subQ0}),-1.0]])]});}
            var Q2;
            {var subQ5=sQuery(id+"F19.wireOp",EDGE,"E88");Q2=makeQuery(id+"F19.imprint","IMPRINT",FACE,{"disambiguationData":[TD([[makeQuery(id+"F19.imprint","IMPRINT",EDGE,{"derivedFrom":subQ5}),-1.0]])]});}
            extrude(context, id + "F20", {"entities" : qUnion([Q0, Q1, Q2]), "operationType" : NewBodyOperationType.REMOVE, "oppositeDirection" : true, "depth" : 4 * mm});
        }
        {
            var Q0;
            Q0=makeQuery(id+"F18.boolean.opBoolean","MERGE",EDGE,{"derivedFrom":[makeQuery(id+"F18.opExtrude","CAP_EDGE",EDGE,{"disambiguationData":[OSD([sQuery(id+"F15.wireOp",EDGE,"E38"),sQuery(id+"F15.wireOp",EDGE,"E39")])],"isStart":false}),makeQuery(id+"F18.opExtrude","CAP_EDGE",EDGE,{"disambiguationData":[OSD([sQuery(id+"F17.wireOp",EDGE,"E53"),sQuery(id+"F17.wireOp",EDGE,"E61")])],"isStart":false})]});
            var Q1;
            Q1=makeQuery(id+"F20.boolean.opBoolean","COPY",EDGE,{"derivedFrom":makeQuery(id+"F20.opExtrude","CAP_EDGE",EDGE,{"disambiguationData":[OSD([sQuery(id+"F19.wireOp",EDGE,"E91")])],"isStart":true})});
            var Q2;
            Q2=makeQuery(id+"F20.boolean.opBoolean","COPY",EDGE,{"derivedFrom":makeQuery(id+"F20.opExtrude","CAP_EDGE",EDGE,{"disambiguationData":[OSD([sQuery(id+"F19.wireOp",EDGE,"E87")])],"isStart":true})});
            var Q3;
            Q3=makeQuery(id+"F18.opExtrude","CAP_EDGE",EDGE,{"disambiguationData":[OSD([sQuery(id+"F17.wireOp",EDGE,"E62"),sQuery(id+"F17.wireOp",EDGE,"E78")])],"isStart":false});
            var Q4;
            Q4=makeQuery(id+"F18.opExtrude","CAP_EDGE",EDGE,{"disambiguationData":[OSD([sQuery(id+"F17.wireOp",EDGE,"E55")])],"isStart":false});
            var Q5;
            Q5=makeQuery(id+"F18.opExtrude","CAP_EDGE",EDGE,{"disambiguationData":[OSD([sQuery(id+"F17.wireOp",EDGE,"E56")])],"isStart":false});
            var Q6;
            Q6=makeQuery(id+"F18.opExtrude","CAP_EDGE",EDGE,{"disambiguationData":[OSD([sQuery(id+"F17.wireOp",EDGE,"E57")])],"isStart":false});
            var Q7;
            Q7=makeQuery(id+"F18.opExtrude","CAP_EDGE",EDGE,{"disambiguationData":[OSD([sQuery(id+"F17.wireOp",EDGE,"E58")])],"isStart":false});
            var Q8;
            Q8=makeQuery(id+"F18.opExtrude","CAP_EDGE",EDGE,{"disambiguationData":[OSD([sQuery(id+"F17.wireOp",EDGE,"E59")])],"isStart":false});
            var Q9;
            Q9=makeQuery(id+"F18.opExtrude","CAP_EDGE",EDGE,{"disambiguationData":[OSD([sQuery(id+"F17.wireOp",EDGE,"E54")])],"isStart":false});
            var Q10;
            Q10=makeQuery(id+"F18.opExtrude","CAP_EDGE",EDGE,{"disambiguationData":[OSD([sQuery(id+"F17.wireOp",EDGE,"E79")])],"isStart":false});
            var Q11;
            Q11=makeQuery(id+"F18.opExtrude","CAP_EDGE",EDGE,{"disambiguationData":[OSD([sQuery(id+"F17.wireOp",EDGE,"E80")])],"isStart":false});
            var Q12;
            Q12=makeQuery(id+"F18.opExtrude","CAP_EDGE",EDGE,{"disambiguationData":[OSD([sQuery(id+"F17.wireOp",EDGE,"E81")])],"isStart":false});
            var Q13;
            Q13=makeQuery(id+"F18.opExtrude","CAP_EDGE",EDGE,{"disambiguationData":[OSD([sQuery(id+"F17.wireOp",EDGE,"E82")])],"isStart":false});
            var Q14;
            Q14=makeQuery(id+"F18.opExtrude","CAP_EDGE",EDGE,{"disambiguationData":[OSD([sQuery(id+"F17.wireOp",EDGE,"E83")])],"isStart":false});
            var Q15;
            Q15=makeQuery(id+"F18.opExtrude","CAP_EDGE",EDGE,{"disambiguationData":[OSD([sQuery(id+"F17.wireOp",EDGE,"E84")])],"isStart":false});
            fillet(context, id + "F21", {"entities" : qUnion([Q0, Q1, Q2, Q3, Q4, Q5, Q6, Q7, Q8, Q9, Q10, Q11, Q12, Q13, Q14, Q15]), "radius" : 1 * mm, "tangentPropagation" : true, "allowEdgeOverflow" : false});
        }
        {
            var Q0;
            Q0=makeQuery(id+"F4.boolean.opBoolean","MERGE",FACE,{"derivedFrom":[makeQuery(id+"F1.opExtrude","CAP_FACE",FACE,{"disambiguationData":[OSD([sQuery(id+"F0.wireOp",EDGE,"E0"),sQuery(id+"F0.wireOp",EDGE,"E1"),sQuery(id+"F0.wireOp",EDGE,"E2"),sQuery(id+"F0.wireOp",EDGE,"E5"),sQuery(id+"F0.wireOp",EDGE,"E7.left"),sQuery(id+"F0.wireOp",EDGE,"E7.right"),sQuery(id+"F0.wireOp",EDGE,"E8.bottom"),sQuery(id+"F0.wireOp",EDGE,"E8.left"),sQuery(id+"F0.wireOp",EDGE,"E8.right"),sQuery(id+"F0.wireOp",EDGE,"E9"),sQuery(id+"F0.wireOp",EDGE,"E10")])],"isStart":false}),makeQuery(id+"F4.opExtrude","CAP_FACE",FACE,{"disambiguationData":[OSD([sQuery(id+"F3.wireOp",EDGE,"E12.bottom"),sQuery(id+"F3.wireOp",EDGE,"E12.top"),sQuery(id+"F3.wireOp",EDGE,"E12.left"),sQuery(id+"F3.wireOp",EDGE,"E12.right")])],"isStart":false}),makeQuery(id+"F4.opExtrude","CAP_FACE",FACE,{"disambiguationData":[OSD([sQuery(id+"F3.wireOp",EDGE,"E13.bottom"),sQuery(id+"F3.wireOp",EDGE,"E13.top"),sQuery(id+"F3.wireOp",EDGE,"E13.left"),sQuery(id+"F3.wireOp",EDGE,"E13.right")])],"isStart":false})]});
            var sketch = newSketch(context, id + "F22", { "sketchPlane" : qUnion([Q0])});
            skCircle(sketch, "E95", {"center": v(0, 0) * mm, "radius": 27 * mm});
            skLineSegment(sketch, "E96", {"start": v(-41.97, 26.95) * mm, "end": v(44.28, 26.95) * mm, "construction": true});
            skLineSegment(sketch, "E97", {"start": v(-52.53, -16) * mm, "end": v(44.71, -16) * mm, "construction": true});
            skLineSegment(sketch, "E98", {"start": v(-27, 26.95) * mm, "end": v(-27, -16) * mm});
            skPoint(sketch, "E99", {"position": v(-27, 0) * mm});
            skLineSegment(sketch, "E100", {"start": v(27, 26.95) * mm, "end": v(27, 0) * mm});
            skLineSegment(sketch, "E101", {"start": v(27, 0) * mm, "end": v(27, -16) * mm});
            skLineSegment(sketch, "E102", {"start": v(-27, 26.95) * mm, "end": v(-20, 26.95) * mm});
            skLineSegment(sketch, "E103", {"start": v(-20, 26.95) * mm, "end": v(-20, 18.14) * mm});
            skLineSegment(sketch, "E104", {"start": v(-27, -16) * mm, "end": v(-21.75, -16) * mm});
            skLineSegment(sketch, "E105", {"start": v(27, 26.95) * mm, "end": v(20, 26.95) * mm});
            skLineSegment(sketch, "E106", {"start": v(20, 26.95) * mm, "end": v(20, 18.14) * mm});
            skLineSegment(sketch, "E107", {"start": v(27, -16) * mm, "end": v(21.75, -16) * mm});
            skSolve(sketch);
        }
        {
            var Q0;
            {var subQ4=sQuery(id+"F22.wireOp",EDGE,"E102");Q0=makeQuery(id+"F22.imprint","IMPRINT",FACE,{"disambiguationData":[TD([[makeQuery(id+"F22.imprint","IMPRINT",EDGE,{"derivedFrom":subQ4}),-1.0]])]});}
            var Q1;
            {var subQ0=sQuery(id+"F22.wireOp",EDGE,"E104");Q1=makeQuery(id+"F22.imprint","IMPRINT",FACE,{"disambiguationData":[TD([[makeQuery(id+"F22.imprint","IMPRINT",EDGE,{"derivedFrom":subQ0}),1.0]])]});}
            var Q2;
            {var subQ2=sQuery(id+"F22.wireOp",EDGE,"E100");Q2=makeQuery(id+"F22.imprint","IMPRINT",FACE,{"disambiguationData":[TD([[makeQuery(id+"F22.imprint","IMPRINT",EDGE,{"derivedFrom":subQ2}),-1.0]])]});}
            var Q3;
            {var subQ2=sQuery(id+"F22.wireOp",EDGE,"E101");Q3=makeQuery(id+"F22.imprint","IMPRINT",FACE,{"disambiguationData":[TD([[makeQuery(id+"F22.imprint","IMPRINT",EDGE,{"derivedFrom":subQ2}),-1.0]])]});}
            var Q4;
            {var subQ0=sQuery(id+"F7.wireOp",EDGE,"E15.top");Q4=makeQuery(id+"F14.boolean.opBoolean","MERGE",FACE,{"derivedFrom":[makeQuery(id+"F9.boolean.opBoolean","MERGE",FACE,{"derivedFrom":[makeQuery(id+"F8.opExtrude","SWEPT_FACE",FACE,{"disambiguationData":[OSD([subQ0])]}),makeQuery(id+"F9.opExtrude","SWEPT_FACE",FACE,{"disambiguationData":[OSD([subQ0])]})]}),makeQuery(id+"F14.opExtrude","CAP_FACE",FACE,{"disambiguationData":[OSD([sQuery(id+"F10.wireOp",EDGE,"E24.top")]),ownerDisambiguation([makeQuery(id+"F14.opExtrude","SWEPT_BODY",BODY,{"disambiguationData":[OSD([sQuery(id+"F0.wireOp",EDGE,"E7.left"),sQuery(id+"F0.wireOp",EDGE,"E8.top"),sQuery(id+"F0.wireOp",EDGE,"E9"),sQuery(id+"F13.wireOp",EDGE,"E25"),sQuery(id+"F13.wireOp",EDGE,"E26"),sQuery(id+"F13.wireOp",EDGE,"E31"),sQuery(id+"F13.wireOp",EDGE,"E34")])]})])],"isStart":false})]});}
            extrude(context, id + "F23", {"entities" : qUnion([Q0, Q1, Q2, Q3]), "operationType" : NewBodyOperationType.ADD, "endBound" : BoundingType.UP_TO_SURFACE, "oppositeDirection" : true, "endBoundEntityFace" : qUnion([Q4]), "depth" : 25 * mm});
        }
        {
            var Q0;
            {var subQ0=sQuery(id+"F15.wireOp",EDGE,"E38");Q0=makeQuery(id+"F18.boolean.opBoolean","MERGE",FACE,{"derivedFrom":[makeQuery(id+"F18.opExtrude","CAP_FACE",FACE,{"disambiguationData":[OSD([subQ0])],"isStart":false}),makeQuery(id+"F18.opExtrude","CAP_FACE",FACE,{"disambiguationData":[OSD([sQuery(id+"F0.wireOp",EDGE,"E1"),sQuery(id+"F13.wireOp",EDGE,"E26"),subQ0,sQuery(id+"F17.wireOp",EDGE,"E46"),sQuery(id+"F17.wireOp",EDGE,"E53"),sQuery(id+"F17.wireOp",EDGE,"E54"),sQuery(id+"F17.wireOp",EDGE,"E55"),sQuery(id+"F17.wireOp",EDGE,"E56"),sQuery(id+"F17.wireOp",EDGE,"E57"),sQuery(id+"F17.wireOp",EDGE,"E58"),sQuery(id+"F17.wireOp",EDGE,"E59"),sQuery(id+"F17.wireOp",EDGE,"E60"),sQuery(id+"F17.wireOp",EDGE,"E61")])],"isStart":false})]});}
            var sketch = newSketch(context, id + "F24", { "sketchPlane" : qUnion([Q0])});
            skLineSegment(sketch, "E108.bottom", {"start": v(-36.19, -1.42) * mm, "end": v(38.76, -1.42) * mm});
            skLineSegment(sketch, "E108.top", {"start": v(-36.19, -28.7) * mm, "end": v(38.76, -28.7) * mm});
            skLineSegment(sketch, "E108.left", {"start": v(-36.19, -1.42) * mm, "end": v(-36.19, -28.7) * mm});
            skLineSegment(sketch, "E108.right", {"start": v(38.76, -1.42) * mm, "end": v(38.76, -28.7) * mm});
            skSolve(sketch);
        }
        {
            var Q0;
            Q0=makeQuery(id+"F24.imprint","IMPRINT",FACE,{"disambiguationData":[TD([[makeQuery(id+"F24.imprint","IMPRINT",EDGE,{"derivedFrom":sQuery(id+"F24.wireOp",EDGE,"E108.bottom")}),-1.0]])]});
            var Q1;
            {var subQ1=sQuery(id+"F17.wireOp",EDGE,"E60");Q1=makeQuery(id+"F24.imprint","IMPRINT",FACE,{"disambiguationData":[TD([[makeQuery(id+"F24.imprint","IMPRINT",EDGE,{"derivedFrom":makeQuery(id+"F18.opExtrude","CAP_EDGE",EDGE,{"disambiguationData":[OSD([subQ1])],"isStart":false})}),-1.0]])]});}
            extrude(context, id + "F25", {"entities" : qUnion([Q0, Q1]), "operationType" : NewBodyOperationType.REMOVE, "depth" : 10 * mm});
        }
        {
            var Q0;
            {var subQ0=sQuery(id+"F22.wireOp",EDGE,"E98");var subQ1=sQuery(id+"F22.wireOp",EDGE,"E95");Q0=makeQuery(id+"F23.boolean.opBoolean","MERGE",FACE,{"derivedFrom":[makeQuery(id+"F1.opExtrude","CAP_FACE",FACE,{"disambiguationData":[OSD([sQuery(id+"F0.wireOp",EDGE,"E0"),sQuery(id+"F0.wireOp",EDGE,"E1"),sQuery(id+"F0.wireOp",EDGE,"E2"),sQuery(id+"F0.wireOp",EDGE,"E5"),sQuery(id+"F0.wireOp",EDGE,"E7.left"),sQuery(id+"F0.wireOp",EDGE,"E7.right"),sQuery(id+"F0.wireOp",EDGE,"E8.bottom"),sQuery(id+"F0.wireOp",EDGE,"E8.left"),sQuery(id+"F0.wireOp",EDGE,"E8.right"),sQuery(id+"F0.wireOp",EDGE,"E9"),sQuery(id+"F0.wireOp",EDGE,"E10")])],"isStart":false}),makeQuery(id+"F23.opExtrude","CAP_FACE",FACE,{"disambiguationData":[OSD([subQ1,sQuery(id+"F22.wireOp",EDGE,"E101"),sQuery(id+"F22.wireOp",EDGE,"E107")])],"isStart":true}),makeQuery(id+"F23.opExtrude","CAP_FACE",FACE,{"disambiguationData":[OSD([subQ1,sQuery(id+"F22.wireOp",EDGE,"E100"),sQuery(id+"F22.wireOp",EDGE,"E105"),sQuery(id+"F22.wireOp",EDGE,"E106")])],"isStart":true}),makeQuery(id+"F23.opExtrude","CAP_FACE",FACE,{"disambiguationData":[OSD([subQ1,subQ0,sQuery(id+"F22.wireOp",EDGE,"E102"),sQuery(id+"F22.wireOp",EDGE,"E103")])],"isStart":true}),makeQuery(id+"F23.opExtrude","CAP_FACE",FACE,{"disambiguationData":[OSD([subQ1,subQ0,sQuery(id+"F22.wireOp",EDGE,"E104")])],"isStart":true})]});}
            var sketch = newSketch(context, id + "F26", { "sketchPlane" : qUnion([Q0])});
            skLineSegment(sketch, "E109.left", {"start": v(-27, 30.33) * mm, "end": v(-27, -21) * mm});
            skLineSegment(sketch, "E109.right", {"start": v(27, 30) * mm, "end": v(27, -21) * mm});
            skLineSegment(sketch, "E110", {"start": v(-27, -21) * mm, "end": v(0, -34) * mm});
            skLineSegment(sketch, "E111", {"start": v(0, -34) * mm, "end": v(27, -21) * mm});
            skLineSegment(sketch, "E112", {"start": v(-27, 30.33) * mm, "end": v(0, 56) * mm});
            skLineSegment(sketch, "E113", {"start": v(0, 56) * mm, "end": v(27, 30) * mm});
            skLineSegment(sketch, "E114.left", {"start": v(-30, 33) * mm, "end": v(-30, -20.71) * mm});
            skLineSegment(sketch, "E114.right", {"start": v(30, 33) * mm, "end": v(30, -20.71) * mm});
            skLineSegment(sketch, "E115.top", {"start": v(-30, 94) * mm, "end": v(30, 94) * mm});
            skLineSegment(sketch, "E115.left", {"start": v(-30, 33) * mm, "end": v(-30, 94) * mm});
            skLineSegment(sketch, "E115.right", {"start": v(30, 33) * mm, "end": v(30, 94) * mm});
            skLineSegment(sketch, "E116.top", {"start": v(-30, -72) * mm, "end": v(30, -72) * mm});
            skLineSegment(sketch, "E116.left", {"start": v(-30, -20.71) * mm, "end": v(-30, -72) * mm});
            skLineSegment(sketch, "E116.right", {"start": v(30, -20.71) * mm, "end": v(30, -72) * mm});
            skCircle(sketch, "E117", {"center": v(0, 89) * mm, "radius": 2.65 * mm});
            skCircle(sketch, "E118", {"center": v(0, -67) * mm, "radius": 2.65 * mm});
            skLineSegment(sketch, "E119", {"start": v(0, 59) * mm, "end": v(-30, 30.48) * mm});
            skLineSegment(sketch, "E120", {"start": v(0, 59) * mm, "end": v(30, 30.11) * mm});
            skLineSegment(sketch, "E121", {"start": v(0, -37) * mm, "end": v(30, -22.56) * mm});
            skLineSegment(sketch, "E122", {"start": v(27, -21) * mm, "end": v(-27, -21) * mm});
            skLineSegment(sketch, "E123", {"start": v(0, -37) * mm, "end": v(-30, -22.56) * mm});
            skSolve(sketch);
        }
        {
            var Q0;
            Q0=makeQuery(id+"F26.imprint","IMPRINT",FACE,{"disambiguationData":[TD([[makeQuery(id+"F26.imprint","IMPRINT",EDGE,{"derivedFrom":sQuery(id+"F26.wireOp",EDGE,"2IyW3l2o-hvqG-MqSw-vBOU-l3ZVUqYCPLjH")}),1.0]])]});
            var Q1;
            {var subQ3=sQuery(id+"F26.wireOp",EDGE,"E110");Q1=makeQuery(id+"F26.imprint","IMPRINT",FACE,{"disambiguationData":[TD([[makeQuery(id+"F26.imprint","IMPRINT",EDGE,{"derivedFrom":subQ3}),-1.0]])]});}
            var Q2;
            Q2=makeQuery(id+"F26.imprint","IMPRINT",FACE,{"disambiguationData":[TD([[makeQuery(id+"F26.imprint","IMPRINT",EDGE,{"derivedFrom":sQuery(id+"F26.wireOp",EDGE,"JjKzvuAu-OaxP-0XJC-EEOT-jw4UJeidf5hy")}),-1.0]])]});
            var Q3;
            Q3=makeQuery(id+"F26.imprint","IMPRINT",FACE,{"disambiguationData":[TD([[makeQuery(id+"F26.imprint","IMPRINT",EDGE,{"derivedFrom":sQuery(id+"F26.wireOp",EDGE,"E115.top")}),-1.0]])]});
            var Q4;
            {var subQ1=sQuery(id+"F26.wireOp",EDGE,"E116.top");Q4=makeQuery(id+"F26.imprint","IMPRINT",FACE,{"disambiguationData":[TD([[makeQuery(id+"F26.imprint","IMPRINT",EDGE,{"derivedFrom":subQ1}),1.0]])]});}
            extrude(context, id + "F27", {"entities" : qUnion([Q0, Q1, Q2, Q3, Q4]), "oppositeDirection" : true, "depth" : 3 * mm});
        }
        {
            var Q0;
            {var subQ3=sQuery(id+"F26.wireOp",EDGE,"E110");Q0=makeQuery(id+"F26.imprint","IMPRINT",FACE,{"disambiguationData":[TD([[makeQuery(id+"F26.imprint","IMPRINT",EDGE,{"derivedFrom":subQ3}),-1.0]])]});}
            var Q1;
            {var subQ0=sQuery(id+"F22.wireOp",EDGE,"E98");var subQ1=sQuery(id+"F22.wireOp",EDGE,"E95");var subQ2=sQuery(id+"F7.wireOp",EDGE,"E15.top");Q1=makeQuery(id+"F23.boolean.opBoolean","MERGE",FACE,{"derivedFrom":[makeQuery(id+"F14.boolean.opBoolean","MERGE",FACE,{"derivedFrom":[makeQuery(id+"F9.boolean.opBoolean","MERGE",FACE,{"derivedFrom":[makeQuery(id+"F8.opExtrude","SWEPT_FACE",FACE,{"disambiguationData":[OSD([subQ2])]}),makeQuery(id+"F9.opExtrude","SWEPT_FACE",FACE,{"disambiguationData":[OSD([subQ2])]})]}),makeQuery(id+"F14.opExtrude","CAP_FACE",FACE,{"disambiguationData":[OSD([sQuery(id+"F10.wireOp",EDGE,"E24.top")]),OD(0.0)],"isStart":false})]}),makeQuery(id+"F23.opExtrude","CAP_FACE",FACE,{"disambiguationData":[OSD([subQ1,subQ0,sQuery(id+"F22.wireOp",EDGE,"E102"),sQuery(id+"F22.wireOp",EDGE,"E103")])],"isStart":false}),makeQuery(id+"F23.opExtrude","CAP_FACE",FACE,{"disambiguationData":[OSD([subQ1,subQ0,sQuery(id+"F22.wireOp",EDGE,"E104")])],"isStart":false})]});}
            extrude(context, id + "F28", {"entities" : qUnion([Q0]), "operationType" : NewBodyOperationType.ADD, "endBound" : BoundingType.UP_TO_SURFACE, "oppositeDirection" : true, "endBoundEntityFace" : qUnion([Q1]), "depth" : 25 * mm});
        }
        {
            var Q0;
            Q0=qCreatedBy(makeId("Right.planeOp"),FACE);
            var sketch = newSketch(context, id + "F29", { "sketchPlane" : qUnion([Q0])});
            skLineSegment(sketch, "E124", {"start": v(59, -51.01) * mm, "end": v(59, 27.73) * mm, "construction": true});
            skLineSegment(sketch, "E125", {"start": v(86.5, -31) * mm, "end": v(-16.9, -31) * mm, "construction": true});
            skLineSegment(sketch, "E126", {"start": v(30.48, 33.24) * mm, "end": v(30.48, -51.23) * mm, "construction": true});
            skLineSegment(sketch, "E127", {"start": v(59, 0) * mm, "end": v(30.48, -31) * mm});
            skLineSegment(sketch, "E128", {"start": v(30.48, -31) * mm, "end": v(59, -31) * mm});
            skLineSegment(sketch, "E129", {"start": v(59, -31) * mm, "end": v(59, 0) * mm});
            skSolve(sketch);
        }
        {
            var Q0;
            Q0=makeQuery(id+"F29.imprint","IMPRINT",FACE,{"disambiguationData":[TD([[makeQuery(id+"F29.imprint","IMPRINT",EDGE,{"derivedFrom":sQuery(id+"F29.wireOp",EDGE,"E127")}),1.0]])]});
            extrude(context, id + "F30", {"entities" : qUnion([Q0]), "operationType" : NewBodyOperationType.REMOVE, "endBound" : BoundingType.SYMMETRIC, "oppositeDirection" : true, "depth" : 50 * mm});
        }
        {
            var Q0;
            {var subQ0=sQuery(id+"F26.wireOp",EDGE,"E116.right");var subQ1=sQuery(id+"F26.wireOp",EDGE,"E114.right");Q0=makeQuery(id+"F28.boolean.opBoolean","MERGE",FACE,{"derivedFrom":[makeQuery(id+"F27.opExtrude","SWEPT_FACE",FACE,{"disambiguationData":[OSD([subQ1,sQuery(id+"F26.wireOp",EDGE,"E115.right"),subQ0])]}),makeQuery(id+"F28.opExtrude","SWEPT_FACE",FACE,{"disambiguationData":[OSD([subQ1,subQ0])]})]});}
            var sketch = newSketch(context, id + "F31", { "sketchPlane" : qUnion([Q0])});
            skCircle(sketch, "E130", {"center": v(-6, -6) * mm, "radius": 2.1 * mm});
            skCircle(sketch, "E131", {"center": v(8, -13) * mm, "radius": 2.1 * mm});
            skCircle(sketch, "E132", {"center": v(-6, -6) * mm, "radius": 1.3 * mm});
            skCircle(sketch, "E133", {"center": v(8, -13) * mm, "radius": 1.3 * mm});
            skSolve(sketch);
        }
        {
            var Q0;
            Q0=makeQuery(id+"F31.imprint","IMPRINT",FACE,{"disambiguationData":[TD([[makeQuery(id+"F31.imprint","IMPRINT",EDGE,{"derivedFrom":sQuery(id+"F31.wireOp",EDGE,"E130")}),1.0]])]});
            var Q1;
            Q1=makeQuery(id+"F31.imprint","IMPRINT",FACE,{"disambiguationData":[TD([[makeQuery(id+"F31.imprint","IMPRINT",EDGE,{"derivedFrom":sQuery(id+"F31.wireOp",EDGE,"E132")}),1.0]])]});
            var Q2;
            Q2=makeQuery(id+"F31.imprint","IMPRINT",FACE,{"disambiguationData":[TD([[makeQuery(id+"F31.imprint","IMPRINT",EDGE,{"derivedFrom":sQuery(id+"F31.wireOp",EDGE,"E131")}),1.0]])]});
            var Q3;
            Q3=makeQuery(id+"F31.imprint","IMPRINT",FACE,{"disambiguationData":[TD([[makeQuery(id+"F31.imprint","IMPRINT",EDGE,{"derivedFrom":sQuery(id+"F31.wireOp",EDGE,"E133")}),1.0]])]});
            var Q4;
            {var subQ0=sQuery(id+"F26.wireOp",EDGE,"E116.left");var subQ1=sQuery(id+"F26.wireOp",EDGE,"E114.left");Q4=makeQuery(id+"F28.boolean.opBoolean","MERGE",FACE,{"derivedFrom":[makeQuery(id+"F27.opExtrude","SWEPT_FACE",FACE,{"disambiguationData":[OSD([subQ1,sQuery(id+"F26.wireOp",EDGE,"E115.left"),subQ0])]}),makeQuery(id+"F28.opExtrude","SWEPT_FACE",FACE,{"disambiguationData":[OSD([subQ1,subQ0])]})]});}
            extrude(context, id + "F32", {"entities" : qUnion([Q0, Q1, Q2, Q3]), "operationType" : NewBodyOperationType.REMOVE, "endBound" : BoundingType.UP_TO_SURFACE, "oppositeDirection" : true, "endBoundEntityFace" : qUnion([Q4]), "depth" : 25 * mm});
        }
        {
            var Q0;
            Q0=makeQuery(id+"F31.imprint","IMPRINT",FACE,{"disambiguationData":[TD([[makeQuery(id+"F31.imprint","IMPRINT",EDGE,{"derivedFrom":sQuery(id+"F31.wireOp",EDGE,"E132")}),1.0]])]});
            var Q1;
            Q1=makeQuery(id+"F31.imprint","IMPRINT",FACE,{"disambiguationData":[TD([[makeQuery(id+"F31.imprint","IMPRINT",EDGE,{"derivedFrom":sQuery(id+"F31.wireOp",EDGE,"E133")}),1.0]])]});
            var Q2;
            {var subQ0=sQuery(id+"F26.wireOp",EDGE,"E116.left");var subQ1=sQuery(id+"F26.wireOp",EDGE,"E114.left");Q2=makeQuery(id+"F28.boolean.opBoolean","MERGE",FACE,{"derivedFrom":[makeQuery(id+"F27.opExtrude","SWEPT_FACE",FACE,{"disambiguationData":[OSD([subQ1,sQuery(id+"F26.wireOp",EDGE,"E115.left"),subQ0])]}),makeQuery(id+"F28.opExtrude","SWEPT_FACE",FACE,{"disambiguationData":[OSD([subQ1,subQ0])]})]});}
            extrude(context, id + "F33", {"entities" : qUnion([Q0, Q1]), "operationType" : NewBodyOperationType.REMOVE, "endBound" : BoundingType.UP_TO_SURFACE, "oppositeDirection" : true, "endBoundEntityFace" : qUnion([Q2]), "depth" : 25 * mm});
        }
    });
